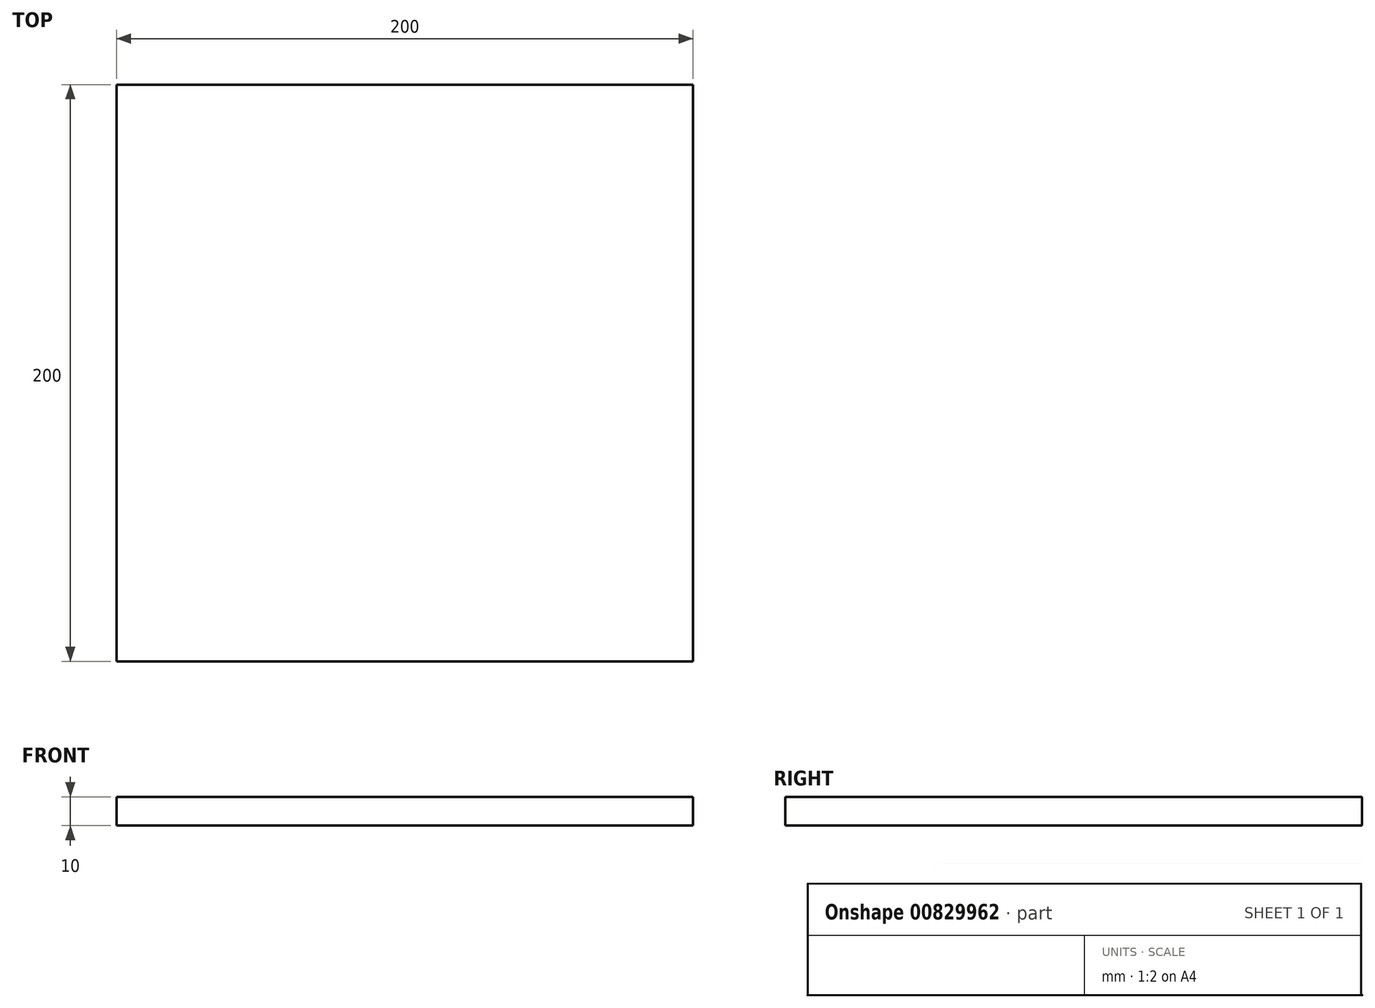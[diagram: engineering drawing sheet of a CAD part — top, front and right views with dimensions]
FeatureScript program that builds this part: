
annotation { "Feature Type Name" : "Feature", "Feature Type Description" : "" }
export const myFeature = defineFeature(function(context is Context, id is Id, definition is map)
    precondition{}
    {
        {
            var Q0;
            Q0=qCreatedBy(makeId("Top.planeOp"),FACE);
            var sketch = newSketch(context, id + "F0", { "sketchPlane" : qUnion([Q0])});
            skLineSegment(sketch, "E0.bottom", {"start": v(-93.56, 100) * mm, "end": v(106.44, 100) * mm});
            skLineSegment(sketch, "E0.top", {"start": v(-93.56, -100) * mm, "end": v(106.44, -100) * mm});
            skLineSegment(sketch, "E0.left", {"start": v(-93.56, 100) * mm, "end": v(-93.56, -100) * mm});
            skLineSegment(sketch, "E0.right", {"start": v(106.44, 100) * mm, "end": v(106.44, -100) * mm});
            skPoint(sketch, "E0.middle", {"position": v(6.44, 0) * mm});
            skLineSegment(sketch, "E1", {"start": v(106.44, 23.2) * mm, "end": v(-93.56, 23.2) * mm});
            skLineSegment(sketch, "E2", {"start": v(106.44, 13.2) * mm, "end": v(-93.56, 13.2) * mm});
            skSolve(sketch);
        }
        {
            var Q0;
            Q0 = qSketchRegion(id + "F0", true);
            extrude(context, id + "F1", {"entities" : qUnion([Q0]), "depth" : 10 * mm, "offsetDistance" : 25 * mm});
        }
    });
